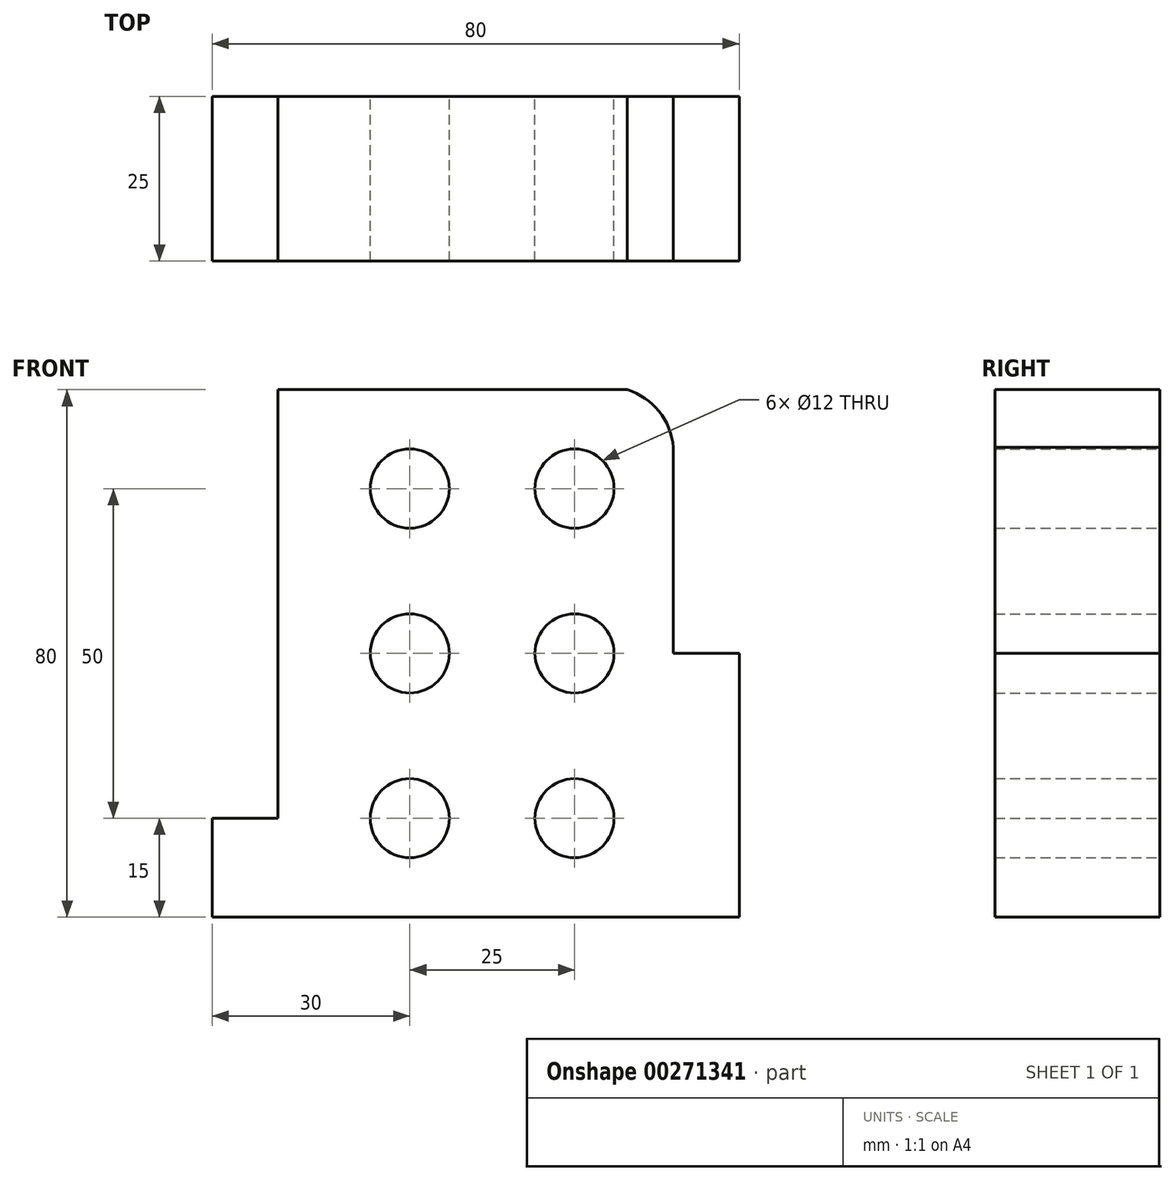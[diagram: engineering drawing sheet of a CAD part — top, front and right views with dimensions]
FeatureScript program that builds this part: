
annotation { "Feature Type Name" : "Feature", "Feature Type Description" : "" }
export const myFeature = defineFeature(function(context is Context, id is Id, definition is map)
    precondition{}
    {
        {
            var Q0;
            Q0=qCreatedBy(makeId("Front.planeOp"),FACE);
            var sketch = newSketch(context, id + "F0", { "sketchPlane" : qUnion([Q0])});
            skLineSegment(sketch, "E0", {"start": v(0, 0) * mm, "end": v(80, 0) * mm});
            skLineSegment(sketch, "E1", {"start": v(0, 0) * mm, "end": v(0, 15) * mm});
            skLineSegment(sketch, "E2", {"start": v(0, 15) * mm, "end": v(10, 15) * mm});
            skLineSegment(sketch, "E3", {"start": v(10, 15) * mm, "end": v(10, 80) * mm});
            skLineSegment(sketch, "E4", {"start": v(80, 0) * mm, "end": v(80, 40) * mm});
            skLineSegment(sketch, "E5", {"start": v(80, 40) * mm, "end": v(70, 40) * mm});
            skLineSegment(sketch, "E6", {"start": v(10, 80) * mm, "end": v(63, 80) * mm});
            skCircle(sketch, "E7", {"center": v(30, 65) * mm, "radius": 6 * mm});
            skCircle(sketch, "E8", {"center": v(55, 65) * mm, "radius": 6 * mm});
            skCircle(sketch, "E9", {"center": v(30, 40) * mm, "radius": 6 * mm});
            skCircle(sketch, "E10", {"center": v(55, 40) * mm, "radius": 6 * mm});
            skCircle(sketch, "E11", {"center": v(30, 15) * mm, "radius": 6 * mm});
            skCircle(sketch, "E12", {"center": v(55, 15) * mm, "radius": 6 * mm});
            skArc(sketch, "E13", {"start": v(70, 71.28) * mm, "mid": v(67.83, 76.71) * mm, "end": v(63, 80) * mm});
            skLineSegment(sketch, "E14", {"start": v(70, 40) * mm, "end": v(70, 71.28) * mm});
            skSolve(sketch);
        }
        {
            var Q0;
            Q0 = qSketchRegion(id + "F0", true);
            extrude(context, id + "F1", {"entities" : qUnion([Q0]), "depth" : 25 * mm});
        }
    });
